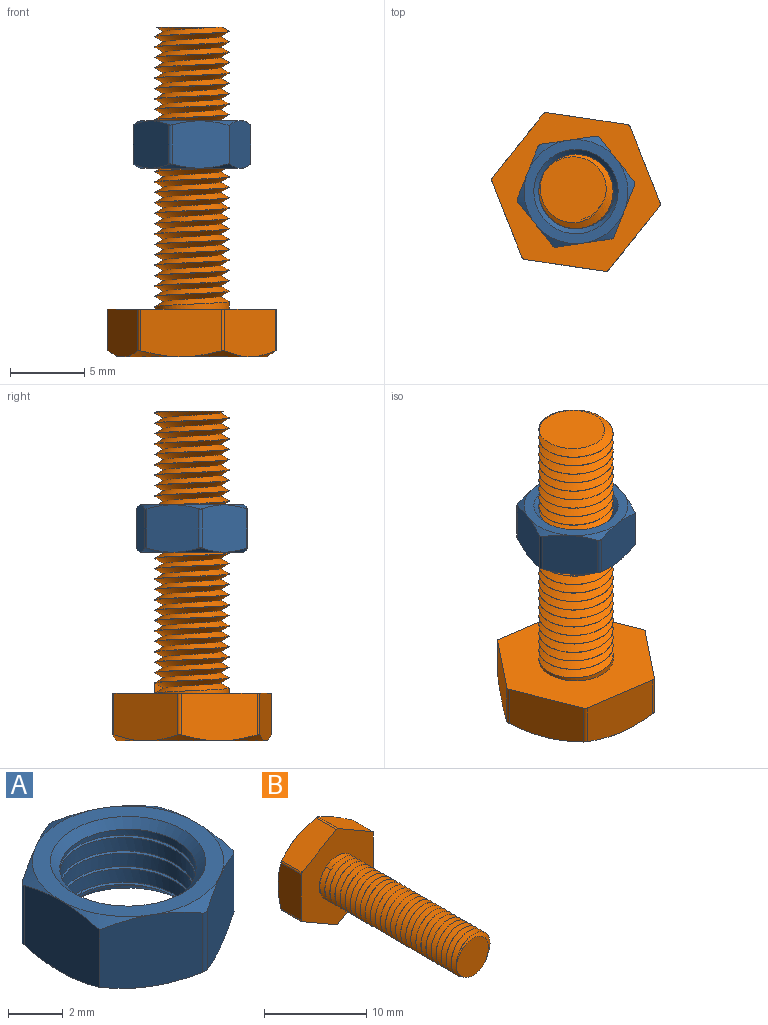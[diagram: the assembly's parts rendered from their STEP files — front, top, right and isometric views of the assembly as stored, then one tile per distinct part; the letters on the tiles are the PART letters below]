
ASSEMBLY  parts=2 mates=1
PART A: 31 faces, bbox 8.3x8.3x3.8 mm
  f0: plane 7x7mm, normal (0,0,1), area 13.2mm2, adj f5,f6,f8,f10,f12,f14,f21
  f1: plane 7x7mm, normal (0,0,-1), area 13.2mm2, adj f3,f4,f7,f9,f11,f13,f23
  f2: cylinder r=2.5mm len=5mm, axis (0,0,-1), area 33.8mm2, adj f21,f22,f23,f24,f25
  f3: cone r=5.79mm half-angle=60deg, axis (0,0,1), area 1.2mm2, adj f1,f15,f16
  f4: cone r=5.79mm half-angle=60deg, axis (0,0,1), area 0.8mm2, adj f1,f15,f20,f30
  f5: cone r=5.79mm half-angle=60deg, axis (0,0,-1), area 1.2mm2, adj f0,f15,f16
  f6: cone r=5.79mm half-angle=60deg, axis (0,0,-1), area 0.8mm2, adj f0,f15,f20,f30
  f7: cone r=5.79mm half-angle=60deg, axis (0,0,1), area 0.8mm2, adj f1,f16,f17,f29
  f8: cone r=5.79mm half-angle=60deg, axis (0,0,-1), area 0.8mm2, adj f0,f16,f17,f29
  f9: cone r=5.79mm half-angle=60deg, axis (0,0,1), area 0.8mm2, adj f1,f17,f18,f28
  f10: cone r=5.79mm half-angle=60deg, axis (0,0,-1), area 0.8mm2, adj f0,f17,f18,f28
  f11: cone r=5.79mm half-angle=60deg, axis (0,0,1), area 0.8mm2, adj f1,f18,f19,f27
  f12: cone r=5.79mm half-angle=60deg, axis (0,0,-1), area 0.8mm2, adj f0,f18,f19,f27
  f13: cone r=5.79mm half-angle=60deg, axis (0,0,1), area 0.8mm2, adj f1,f19,f20,f26
  f14: cone r=5.79mm half-angle=60deg, axis (0,0,-1), area 0.8mm2, adj f0,f19,f20,f26
  f15: plane 3.71x3.54mm, normal (-0.5,-0.87,0), area 11.7mm2, adj f3,f4,f5,f6,f16,f30
  f16: plane 4.23x3.53mm, normal (-1,0,0), area 11.7mm2, adj f3,f5,f7,f8,f15,f29
  f17: plane 3.26x3.21mm, normal (-0.5,0.87,0), area 11.3mm2, adj f7,f8,f9,f10,f28,f29
  f18: plane 3.26x3.21mm, normal (0.5,0.87,0), area 11.3mm2, adj f9,f10,f11,f12,f27,f28
  f19: plane 3.76x3.2mm, normal (1,0,0), area 11.3mm2, adj f11,f12,f13,f14,f26,f27
  f20: plane 3.26x3.21mm, normal (0.5,-0.87,0), area 11.3mm2, adj f4,f6,f13,f14,f26,f30
  f21: cone r=2.5mm half-angle=45deg, axis (0,0,1), area 7.9mm2, adj f0,f2,f24,f25
  f22: cone r=2.84mm half-angle=45deg, axis (0,0,-1), area 0.1mm2, adj f2,f23,f24
  f23: cone r=2.84mm half-angle=45deg, axis (0,0,-1), area 7.8mm2, adj f1,f2,f22,f25
  f24: bspline ~5.99x5.19mm, area 6.4mm2, adj f2,f21,f22,f25
  f25: bspline ~5.99x5.19mm, area 6.4mm2, adj f2,f21,f23,f24
  f26: cylinder r=0.25mm len=2.66mm, axis (0,0,-1), area 0.7mm2, adj f13,f14,f19,f20
  f27: cylinder r=0.25mm len=2.66mm, axis (0,0,-1), area 0.7mm2, adj f11,f12,f18,f19
  f28: cylinder r=0.25mm len=2.66mm, axis (0,0,-1), area 0.7mm2, adj f9,f10,f17,f18
  f29: cylinder r=0.25mm len=2.66mm, axis (0,0,-1), area 0.7mm2, adj f7,f8,f16,f17
  f30: cylinder r=0.25mm len=2.66mm, axis (0,0,-1), area 0.7mm2, adj f4,f6,f15,f20
PART B: 25 faces, bbox 11.9x23.1x12 mm
  f0: cylinder r=2.5mm len=19mm, axis (0,1,0), area -90.8mm2, adj f7,f15,f16,f17,f18
  f1: plane 4.76x3.2mm, normal (0.5,0,-0.87), area 16.8mm2, adj f7,f9,f13,f19,f24
  f2: plane 5.49x3.2mm, normal (1,0,0), area 16.8mm2, adj f7,f12,f13,f19,f20
  f3: plane 4.76x3.2mm, normal (0.5,0,0.87), area 16.8mm2, adj f7,f11,f12,f20,f21
  f4: plane 4.76x3.2mm, normal (-0.5,0,0.87), area 16.8mm2, adj f7,f10,f11,f21,f22
  f5: plane 5.49x3.2mm, normal (-1,0,0), area 16.8mm2, adj f7,f8,f10,f22,f23
  f6: plane 4.76x3.2mm, normal (-0.5,0,-0.87), area 16.8mm2, adj f7,f8,f9,f23,f24
  f7: plane 11.47x10mm, normal (0,-1,0), area 66.9mm2, adj f0,f1,f2,f3,f4,f5,f6,f17
  f8: cone r=7.29mm half-angle=60deg, axis (0,-1,0), area 1.5mm2, adj f5,f6,f14,f23
  f9: cone r=7.29mm half-angle=60deg, axis (0,-1,0), area 1.5mm2, adj f1,f6,f14,f24
  f10: cone r=7.29mm half-angle=60deg, axis (0,-1,0), area 1.5mm2, adj f4,f5,f14,f22
  f11: cone r=7.29mm half-angle=60deg, axis (0,-1,0), area 1.5mm2, adj f3,f4,f14,f21
  f12: cone r=7.29mm half-angle=60deg, axis (0,-1,0), area 1.5mm2, adj f2,f3,f14,f20
  f13: cone r=7.29mm half-angle=60deg, axis (0,-1,0), area 1.5mm2, adj f1,f2,f14,f19
  f14: plane 10x10mm, normal (0,1,0), area 78.5mm2, adj f8,f9,f10,f11,f12,f13
  f15: plane 4.93x4.92mm, normal (0,-1,0), area 15.4mm2, adj f0,f17,f18
  f16: plane 0.69x0.47mm, normal (-0.78,0,-0.62), area 0.2mm2, adj f0,f17,f18
  f17: bspline ~19.36x5.77mm, area 253.5mm2, adj f0,f7,f15,f16,f18
  f18: bspline ~19.13x5.77mm, area 249.7mm2, adj f0,f15,f16,f17
  f19: cylinder r=0.25mm len=2.79mm, axis (0,1,0), area 0.7mm2, adj f1,f2,f7,f13
  f20: cylinder r=0.25mm len=2.79mm, axis (0,1,0), area 0.7mm2, adj f2,f3,f7,f12
  f21: cylinder r=0.25mm len=2.79mm, axis (0,1,0), area 0.7mm2, adj f3,f4,f7,f11
  f22: cylinder r=0.25mm len=2.79mm, axis (0,1,0), area 0.7mm2, adj f4,f5,f7,f10
  f23: cylinder r=0.25mm len=2.79mm, axis (0,1,0), area 0.7mm2, adj f5,f6,f7,f8
  f24: cylinder r=0.25mm len=2.79mm, axis (0,1,0), area 0.7mm2, adj f1,f6,f7,f9
PLACE A rot(axis=(0,0,1),98.4deg) t=(23.4,-2.26,20.74)mm
PLACE B rot(axis=(-0.9,0.31,-0.31),96.2deg) t=(23.4,-2.26,8.04)mm
MATE cylindrical B.f0 <-> A.f3  axis (0,0,1) through (23.4,-2.26,30.24)mm
